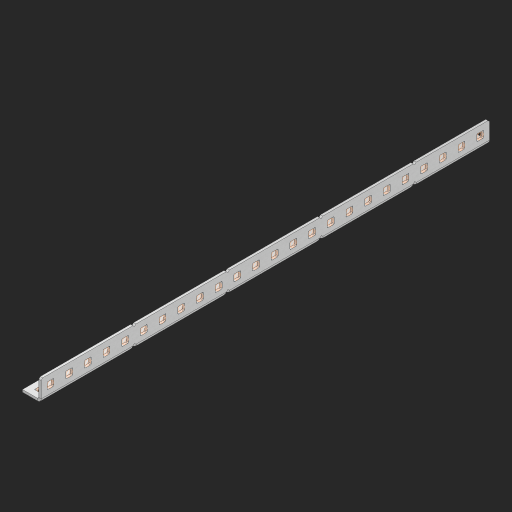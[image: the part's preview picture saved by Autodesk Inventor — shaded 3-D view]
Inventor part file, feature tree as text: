
AUTODESK INVENTOR PART (.ipt)
format: ipt  version: 2023 (Build 270158000, 158)  size: 844,288 bytes
history: native  units: in
note: dims shown in document units (in); Inventor stores cm internally (conversion verified against a paired STEP export)
features: other x53, extrude x47, sheet_metal_op x10, sketch x8, mirror x1, pattern_linear x1, chamfer x1
ambient origin geometry x8: Origin, YZ Plane, XZ Plane, XY Plane, X Axis, Y Axis, Z Axis, Center Point
bodies: Solid1 (feature_tree), Body (feature_tree)
feature tree (121):
  other  "Flange Pattern Plane"
  sheet_metal_op  "Flange Pattern"
  sheet_metal_op  "Body Pattern"
  other  "Arc Length"
  mirror  "Notch Mirror"
  pattern_linear  "Notch Pattern"  Spacing1=0.25in  [1 undecoded]
  chamfer  "End Chamfer"
  extrude  "Half Cut"  Depth=0.0625in
  sketch  "Sketch1"  dims[d0=1.5in]
  other  "Plate1"
  sketch  "Sketch2"  dims[d1=12.0in]
  other  "Plate2"
  sheet_metal_op  "Bend1"
  sheet_metal_op  "Corner1"
  sketch  "Sketch3"  dims[d2=0.0625in]
  other  "Flange Pattern Sketch"
  sketch  "Sketch7"  dims[d3=0.0625in]
  other  "Srf1"
  other  "Srf2"
  sketch  "Sketch8"  dims[d4=0.0312in]
  sketch  "Sketch9"  dims[d5=0.125in]
  other  "Srf91"
  sheet_metal_op  "Body Pattern Sketch"
  other  "Srf92"
  sketch  "Sketch13"  dims[d6=0.0625in]
  sketch  "Sketch14"  dims[d7=0.5in d8=90.0deg d9=0.0312in d10=0.25in d11=0.0625in d12=0.0625in d16=0.182in d17=0.02in d18=0.0625in d19=0.0in d20=0.25in d21=0.25in d46=0.172in d47=1.0in d48=0.0in d49=0.182in d50=0.02in d51=0.25in d52=0.25in d53=0.0625in d54=0.0in d55=0.172in d56=1.0in d57=0.0in d60=9.4488in d62=0.5in d63=0.3937in d65=0.5in d85=0.1473in d86=0.1782in d88=0.04in d89=0.0625in d90=0.0in d91=0.04in d92=0.0491in d95=2.5in d96=0.04in d97=0.25in d98=45.0deg d101=0.0in d102=2.497in d131=0.5in d132=9.4488in d134=0.5in d139=0.5in]
  other  "Srf856"
  other  "Srf1310"
  other  "Srf1311"
  other  "Srf1312"
  other  "Srf1376"
  other  "Srf1377"
  other  "Srf1728"
  other  "Srf1755"
  other  "Srf1878"
  other  "Srf1879"
  other  "Srf1880"
  other  "Srf1881"
  other  "Srf1882"
  other  "Srf1883"
  other  "Srf1884"
  other  "Srf1885"
  other  "Srf1886"
  other  "Srf1887"
  other  "Srf1888"
  other  "Srf1889"
  other  "Srf1890"
  other  "Srf1891"
  other  "Srf1892"
  other  "Srf1893"
  other  "Srf1894"
  other  "Srf1895"
  other  "Srf1942"
  other  "Srf1943"
  other  "Srf1944"
  other  "Srf1945"
  other  "Srf1946"
  other  "Srf1947"
  other  "Srf1948"
  other  "Srf1949"
  other  "Srf1950"
  other  "Srf1951"
  other  "Srf1952"
  other  "Srf1953"
  other  "Srf1954"
  other  "Srf1955"
  other  "Srf1956"
  other  "Srf1957"
  other  "Srf1958"
  other  "Srf1959"
  sheet_metal_op  "Flange Stamp"
  sheet_metal_op  "Flange Circle"
  sheet_metal_op  "Body Stamp"
  sheet_metal_op  "Body Circle"
  sheet_metal_op  "Notch"
  extrude  "ExtrusionSrf2"  Depth=0.0625in
  extrude  "ExtrusionSrf92"  Depth=0.5in
  extrude  "ExtrusionSrf856"  Depth=0.02in
  extrude  "ExtrusionSrf1310"  Depth=0.0625in
  extrude  "ExtrusionSrf1311"  TaperAngle=0.0deg  [1 undecoded]
  extrude  "ExtrusionSrf1312"  Depth=0.5in
  extrude  "ExtrusionSrf1376"  Depth=0.5in
  extrude  "ExtrusionSrf1377"  Depth=0.5in
  extrude  "ExtrusionSrf1728"  Depth=0.5in TaperAngle=0.0deg
  extrude  "ExtrusionSrf1755"  Depth=0.5in
  extrude  "ExtrusionSrf1878"  Depth=0.02in
  extrude  "ExtrusionSrf1879"  Depth=0.5in
  extrude  "ExtrusionSrf1880"  Depth=0.5in
  extrude  "ExtrusionSrf1881"  Depth=0.0625in
  extrude  "ExtrusionSrf1882"  TaperAngle=0.0deg  [1 undecoded]
  extrude  "ExtrusionSrf1883"  Depth=0.5in
  extrude  "ExtrusionSrf1884"  Depth=0.5in TaperAngle=0.0deg
  extrude  "ExtrusionSrf1885"  Depth=0.5in
  extrude  "ExtrusionSrf1886"  Depth=0.5in
  extrude  "ExtrusionSrf1887"  Depth=0.5in
  extrude  "ExtrusionSrf1888"  Depth=0.5in
  extrude  "ExtrusionSrf1889"  Depth=0.5in
  extrude  "ExtrusionSrf1890"  Depth=0.0625in
  extrude  "ExtrusionSrf1891"  TaperAngle=0.0deg  [1 undecoded]
  extrude  "ExtrusionSrf1892"  Depth=0.5in
  extrude  "ExtrusionSrf1893"  Depth=0.5in
  extrude  "ExtrusionSrf1894"  Depth=0.5in
  extrude  "ExtrusionSrf1895"  Depth=0.5in TaperAngle=45.0deg
  extrude  "ExtrusionSrf1942"  TaperAngle=0.0deg  [1 undecoded]
  extrude  "ExtrusionSrf1943"  Depth=0.5in
  extrude  "ExtrusionSrf1944"  Depth=0.5in
  extrude  "ExtrusionSrf1945"  Depth=0.5in
  extrude  "ExtrusionSrf1946"  Depth=0.5in
  extrude  "ExtrusionSrf1947"  Depth=0.5in
  extrude  "ExtrusionSrf1948"  [1 undecoded]
  extrude  "ExtrusionSrf1949"  [1 undecoded]
  extrude  "ExtrusionSrf1950"  [1 undecoded]
  extrude  "ExtrusionSrf1951"  [1 undecoded]
  extrude  "ExtrusionSrf1952"  [1 undecoded]
  extrude  "ExtrusionSrf1953"  [1 undecoded]
  extrude  "ExtrusionSrf1954"  [1 undecoded]
  extrude  "ExtrusionSrf1955"  [1 undecoded]
  extrude  "ExtrusionSrf1956"  [1 undecoded]
  extrude  "ExtrusionSrf1957"  [1 undecoded]
  extrude  "ExtrusionSrf1958"  [1 undecoded]
  extrude  "ExtrusionSrf1959"  [1 undecoded]
note: 17 required parameter values undecoded (feature->parameter linkage not recoverable at this tier; creation-order binding heuristic only, values carry confidence <= 0.55)
